# Revit family: ledtrunking_module_l15-50w-4000-120-dali_542005006600
name_source: partatom
category: Leuchten
revit_build: Autodesk Revit 2016 (Build: 20190508_0715(x64)
units: mm (PartAtom-declared; Revit-internal decimal feet)

## family parameters
Basisbauteil = Fläche
Beim Laden mit Abzugskörper schneiden = Nein
Bemaßung runder Anschluss = Durchmesser verwenden
Gemeinsam genutzt = Nein
Lichtquelle = Nein
Raumberechnungspunkt = Nein
Teiletyp = Normal

## types (1)
- LEDTrunking Module L15-50W-4000-120-DALI (1 x LED, 8000 lm)
    Approval mark = CE, ENEC
    Beschreibung = Professional LED light line solution. Simple installation with snap-in mounting of LED modules and trunks. Huge energy saving up to 65% compared to conventional TL lighting. Integration of 3C Spots possible with 3C Track Module accessory.
    CIE Flux Codes = 45 81 97 99 100
    Control Gear = Electronic ballast
    Height = 40 mm  [stored 0.131234 ft]
    Hersteller = OPPLE
    Lamp Light Flux = 8000 lm
    Lamp count = 1
    Lampe = 1 x LED
    Length = 1499 mm
    Luminous efficacy = 160 lm/W
    ModVariant = Nein
    Modell = 542005006600
    Mounting Place = Ceiling
    Mounting Type = Pendant
    Number of Poles = 1
    OnlyDefault = Ja
    Power Factor = 1
    Product Name = LEDTrunking Module L15-50W-4000-120-DALI
    Product group = Trunking
    ProductGroupID = 930
    Protection Class = Protection class I
    Protection Degree = IP 20
    RLX_Detail_Level = 1
    RlxData = <blob elided: 40357 chars, md5=3c459539>
    Scheinlast = 50 VA
    Socket = socket
    Standby Power = 0 W
    System Light Flux = 8000 lm
    System Power = 50 W
    Typenbild = 542005006600.jpg
    Typenkommentare = Product without accessories
    URL = http://relux.com
    VarID = ---
    Voltage = 0 V
    Vorgabe-Ansicht = 1800 mm
    Weight = 0.00 kg
    Width = 70 mm

note: [stored X ft] marks values corroborated as IEEE doubles in the binary element streams (Revit-internal decimal feet)

## geometry (parser evidence)
native form markers: Sweep x13
no freeform markers — native parametric forms only
